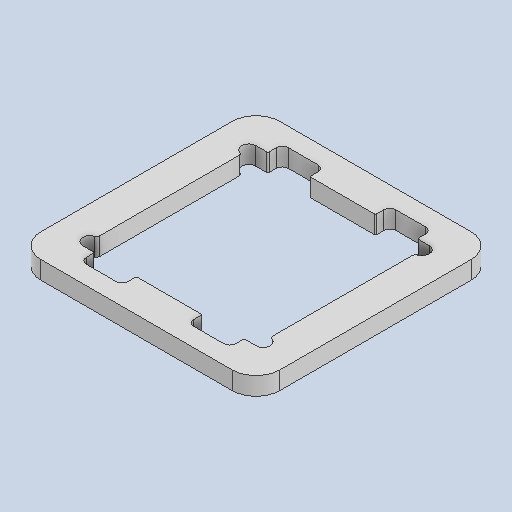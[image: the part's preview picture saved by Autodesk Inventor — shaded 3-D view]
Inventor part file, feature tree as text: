
AUTODESK INVENTOR PART (.ipt)
format: ipt  version: 2025.2 (Build 292293000, 293)  size: 174,080 bytes
history: native  units: mm
features: extrude x1, sketch x1
ambient origin geometry x8: Origin, YZ Plane, XZ Plane, XY Plane, X Axis, Y Axis, Z Axis, Center Point
bodies: Solid1 (feature_tree)
feature tree (2):
  extrude  "Extrusion1"  Depth=14.5mm
  sketch  "Sketch1"  dims[d0=14.5mm d1=14.5mm d2=3.5mm d3=1.2mm d4=1.0mm d5=1.2mm d6=0.1mm d7=0.1mm d8=0.5mm d9=0.25mm d10=2.0mm d11=1.5mm d12=0.0mm d13=20.0mm d14=20.0mm]
